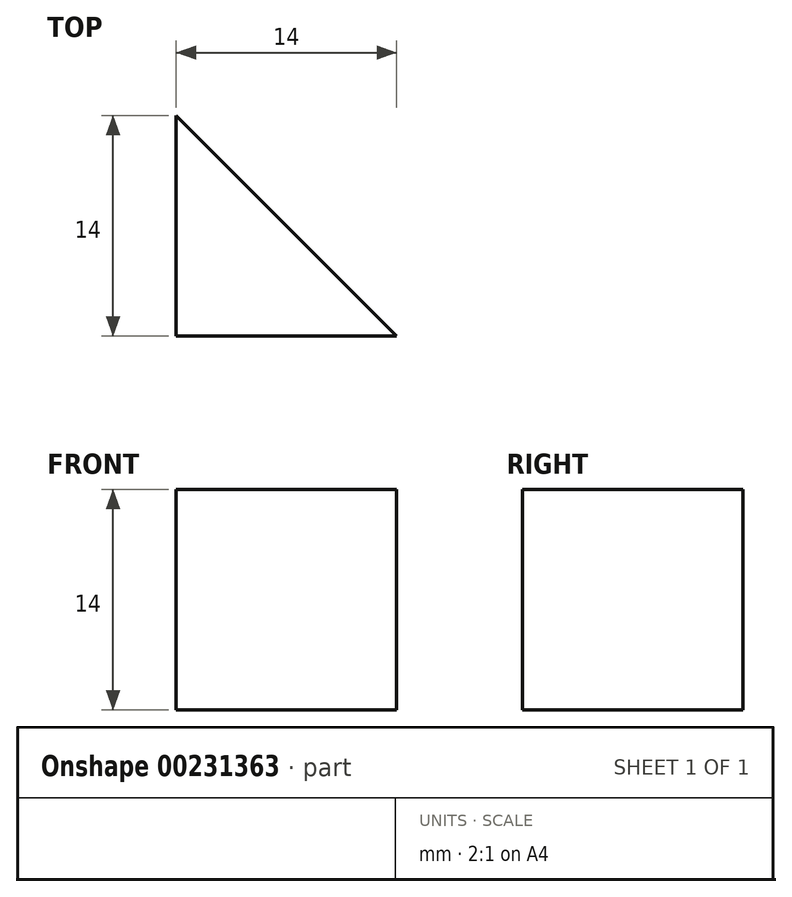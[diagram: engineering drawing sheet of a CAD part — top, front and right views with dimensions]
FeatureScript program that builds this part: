
annotation { "Feature Type Name" : "Feature", "Feature Type Description" : "" }
export const myFeature = defineFeature(function(context is Context, id is Id, definition is map)
    precondition{}
    {
        {
            var Q0;
            Q0=qCreatedBy(makeId("Top.planeOp"),FACE);
            var sketch = newSketch(context, id + "F0", { "sketchPlane" : qUnion([Q0])});
            skLineSegment(sketch, "E0", {"start": v(0, 0) * mm, "end": v(14, 0) * mm});
            skLineSegment(sketch, "E1", {"start": v(14, 0) * mm, "end": v(0, 14) * mm});
            skLineSegment(sketch, "E2", {"start": v(0, 14) * mm, "end": v(0, 0) * mm});
            skSolve(sketch);
        }
        {
            var Q0;
            Q0 = qSketchRegion(id + "F0", true);
            extrude(context, id + "F1", {"entities" : qUnion([Q0]), "depth" : 14 * mm});
        }
    });
